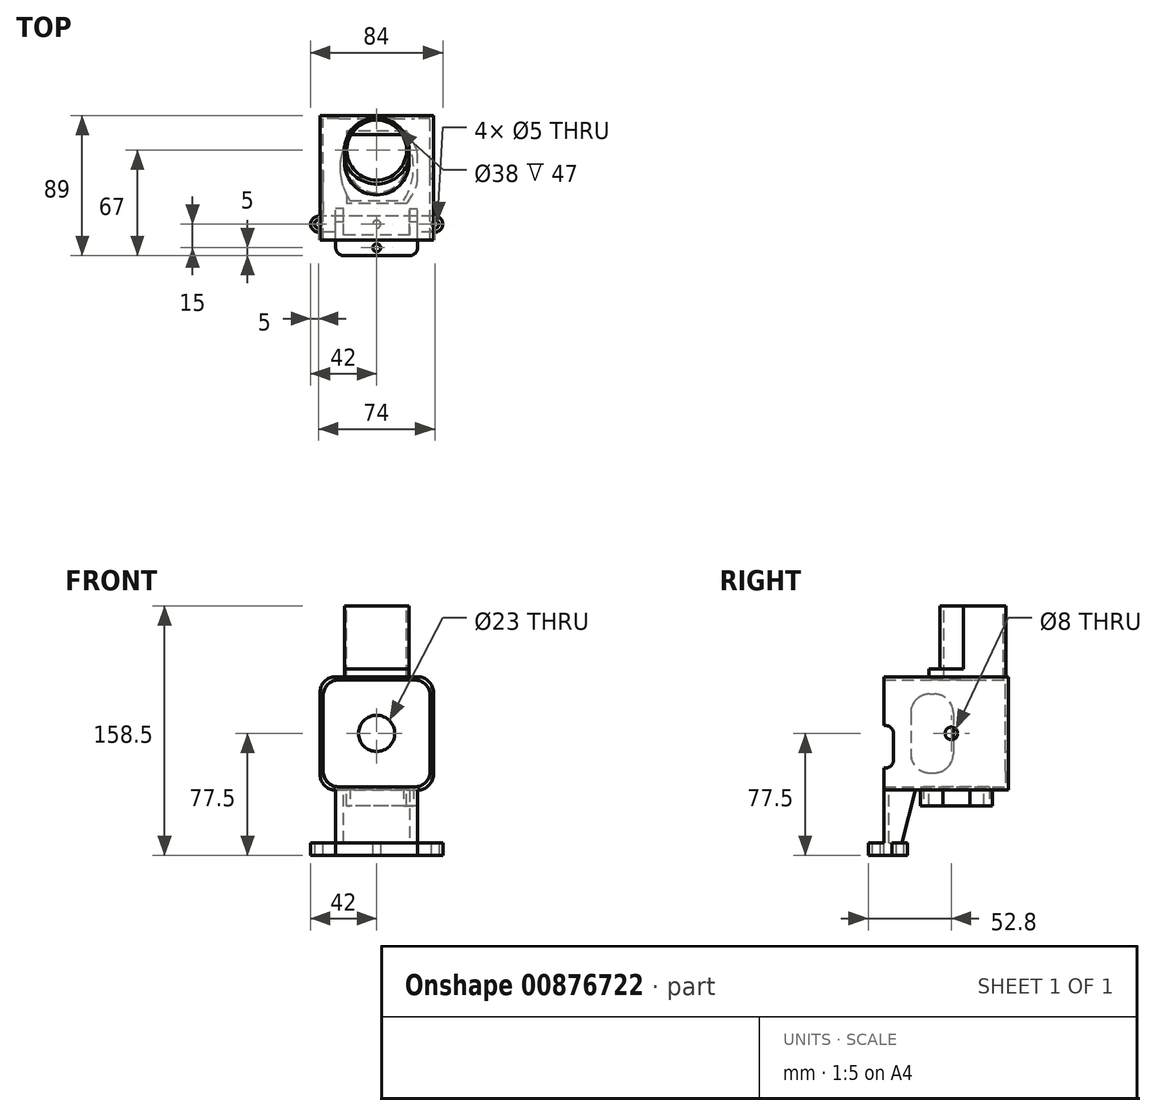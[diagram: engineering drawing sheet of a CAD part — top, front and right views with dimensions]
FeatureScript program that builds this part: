
annotation { "Feature Type Name" : "Feature", "Feature Type Description" : "" }
export const myFeature = defineFeature(function(context is Context, id is Id, definition is map)
    precondition{}
    {
        {
            var Q0;
            Q0=qCreatedBy(makeId("Front.planeOp"),FACE);
            var sketch = newSketch(context, id + "F0", { "sketchPlane" : qUnion([Q0])});
            skLineSegment(sketch, "E0.bottom", {"start": v(-24, -34) * mm, "end": v(24, -34) * mm});
            skLineSegment(sketch, "E0.top", {"start": v(-24, 34) * mm, "end": v(24, 34) * mm});
            skLineSegment(sketch, "E0.left", {"start": v(-34, -24) * mm, "end": v(-34, 24) * mm});
            skLineSegment(sketch, "E0.right", {"start": v(34, -24) * mm, "end": v(34, 24) * mm});
            skPoint(sketch, "E0.middle", {"position": v(0, 0) * mm});
            skLineSegment(sketch, "E1.bottom", {"start": v(-26, 36) * mm, "end": v(26, 36) * mm});
            skLineSegment(sketch, "E1.top", {"start": v(-26, -36) * mm, "end": v(26, -36) * mm});
            skLineSegment(sketch, "E1.left", {"start": v(-36, 26) * mm, "end": v(-36, -26) * mm});
            skLineSegment(sketch, "E1.right", {"start": v(36, 26) * mm, "end": v(36, -26) * mm});
            skCircle(sketch, "E2", {"center": v(0, 0) * mm, "radius": 11.5 * mm});
            skPoint(sketch, "E3.visualSharp", {"position": v(-36, 36) * mm});
            skArc(sketch, "E3.filletArc", {"start": v(-26, 36) * mm, "mid": v(-33.07, 33.07) * mm, "end": v(-36, 26) * mm});
            skPoint(sketch, "E4.visualSharp", {"position": v(-34, 34) * mm});
            skArc(sketch, "E4.filletArc", {"start": v(-24, 34) * mm, "mid": v(-31.07, 31.07) * mm, "end": v(-34, 24) * mm});
            skPoint(sketch, "E5.visualSharp", {"position": v(34, 34) * mm});
            skArc(sketch, "E5.filletArc", {"start": v(34, 24) * mm, "mid": v(31.07, 31.07) * mm, "end": v(24, 34) * mm});
            skPoint(sketch, "E6.visualSharp", {"position": v(36, 36) * mm});
            skArc(sketch, "E6.filletArc", {"start": v(36, 26) * mm, "mid": v(33.07, 33.07) * mm, "end": v(26, 36) * mm});
            skPoint(sketch, "E7.visualSharp", {"position": v(-34, -34) * mm});
            skArc(sketch, "E7.filletArc", {"start": v(-34, -24) * mm, "mid": v(-31.07, -31.07) * mm, "end": v(-24, -34) * mm});
            skPoint(sketch, "E8.visualSharp", {"position": v(-36, -36) * mm});
            skArc(sketch, "E8.filletArc", {"start": v(-36, -26) * mm, "mid": v(-33.07, -33.07) * mm, "end": v(-26, -36) * mm});
            skPoint(sketch, "E9.visualSharp", {"position": v(34, -34) * mm});
            skArc(sketch, "E9.filletArc", {"start": v(24, -34) * mm, "mid": v(31.07, -31.07) * mm, "end": v(34, -24) * mm});
            skPoint(sketch, "E10.visualSharp", {"position": v(36, -36) * mm});
            skArc(sketch, "E10.filletArc", {"start": v(26, -36) * mm, "mid": v(33.07, -33.07) * mm, "end": v(36, -26) * mm});
            skSolve(sketch);
        }
        {
            var Q0;
            Q0=makeQuery(id+"F0.imprint","IMPRINT",FACE,{"disambiguationData":[TD([[makeQuery(id+"F0.imprint","IMPRINT",EDGE,{"derivedFrom":sQuery(id+"F0.wireOp",EDGE,"E0.bottom")}),1.0]])]});
            var Q1;
            Q1=makeQuery(id+"F0.imprint","IMPRINT",FACE,{"disambiguationData":[TD([[makeQuery(id+"F0.imprint","IMPRINT",EDGE,{"derivedFrom":sQuery(id+"F0.wireOp",EDGE,"E0.bottom")}),-1.0]])]});
            extrude(context, id + "F1", {"entities" : qUnion([Q0, Q1]), "depth" : 2 * mm, "offsetDistance" : 25 * mm});
        }
        {
            var Q0;
            Q0=makeQuery(id+"F1.opExtrude","CAP_FACE",FACE,{"disambiguationData":[OSD([sQuery(id+"F0.wireOp",EDGE,"E1.bottom"),sQuery(id+"F0.wireOp",EDGE,"E1.top"),sQuery(id+"F0.wireOp",EDGE,"E1.left"),sQuery(id+"F0.wireOp",EDGE,"E1.right"),sQuery(id+"F0.wireOp",EDGE,"E2"),sQuery(id+"F0.wireOp",EDGE,"E3.filletArc"),sQuery(id+"F0.wireOp",EDGE,"E6.filletArc"),sQuery(id+"F0.wireOp",EDGE,"E8.filletArc"),sQuery(id+"F0.wireOp",EDGE,"E10.filletArc")])],"isStart":false});
            var sketch = newSketch(context, id + "F2", { "sketchPlane" : qUnion([Q0])});
            skLineSegment(sketch, "E11", {"start": v(-26, 36) * mm, "end": v(26, 36) * mm});
            skLineSegment(sketch, "E12", {"start": v(36, 26) * mm, "end": v(36, -26) * mm});
            skLineSegment(sketch, "E13", {"start": v(26, -36) * mm, "end": v(-26, -36) * mm});
            skLineSegment(sketch, "E14", {"start": v(-36, -26) * mm, "end": v(-36, 26) * mm});
            skLineSegment(sketch, "E15.bottom", {"start": v(-24, -34) * mm, "end": v(24, -34) * mm});
            skLineSegment(sketch, "E15.top", {"start": v(-24, 34) * mm, "end": v(24, 34) * mm});
            skLineSegment(sketch, "E15.left", {"start": v(-34, -24) * mm, "end": v(-34, 24) * mm});
            skLineSegment(sketch, "E15.right", {"start": v(34, -24) * mm, "end": v(34, 24) * mm});
            skPoint(sketch, "E15.middle", {"position": v(0, 0) * mm});
            skPoint(sketch, "E16.visualSharp", {"position": v(-34, 34) * mm});
            skArc(sketch, "E16.filletArc", {"start": v(-24, 34) * mm, "mid": v(-31.07, 31.07) * mm, "end": v(-34, 24) * mm});
            skPoint(sketch, "E17.visualSharp", {"position": v(34, 34) * mm});
            skArc(sketch, "E17.filletArc", {"start": v(34, 24) * mm, "mid": v(31.07, 31.07) * mm, "end": v(24, 34) * mm});
            skPoint(sketch, "E18.visualSharp", {"position": v(34, -34) * mm});
            skArc(sketch, "E18.filletArc", {"start": v(24, -34) * mm, "mid": v(31.07, -31.07) * mm, "end": v(34, -24) * mm});
            skPoint(sketch, "E19.visualSharp", {"position": v(-34, -34) * mm});
            skArc(sketch, "E19.filletArc", {"start": v(-34, -24) * mm, "mid": v(-31.07, -31.07) * mm, "end": v(-24, -34) * mm});
            skSolve(sketch);
        }
        {
            var Q0;
            Q0=makeQuery(id+"F2.imprint","IMPRINT",FACE,{"disambiguationData":[TD([[makeQuery(id+"F2.imprint","IMPRINT",EDGE,{"derivedFrom":sQuery(id+"F2.wireOp",EDGE,"E11")}),-1.0]])]});
            extrude(context, id + "F3", {"entities" : qUnion([Q0]), "operationType" : NewBodyOperationType.ADD, "depth" : 77 * mm, "offsetDistance" : 25 * mm});
        }
        {
            var Q0;
            Q0=makeQuery(id+"F3.boolean.opBoolean","MERGE",FACE,{"derivedFrom":[makeQuery(id+"F1.opExtrude","SWEPT_FACE",FACE,{"disambiguationData":[OSD([sQuery(id+"F0.wireOp",EDGE,"E1.left")])]}),makeQuery(id+"F3.opExtrude","SWEPT_FACE",FACE,{"disambiguationData":[OSD([sQuery(id+"F2.wireOp",EDGE,"E14")])]})]});
            var sketch = newSketch(context, id + "F4", { "sketchPlane" : qUnion([Q0])});
            skPoint(sketch, "E20.visualSharp", {"position": v(-64.19, -30) * mm});
            skLineSegment(sketch, "E21.bottom", {"start": v(50, 25) * mm, "end": v(47, 25) * mm});
            skLineSegment(sketch, "E21.top", {"start": v(50, -25) * mm, "end": v(47, -25) * mm});
            skLineSegment(sketch, "E21.left", {"start": v(62, 13) * mm, "end": v(62, -13) * mm});
            skLineSegment(sketch, "E21.right", {"start": v(35, 13) * mm, "end": v(35, -13) * mm});
            skPoint(sketch, "E21.middle", {"position": v(48.5, 0) * mm});
            skPoint(sketch, "E22.visualSharp", {"position": v(62, -25) * mm});
            skArc(sketch, "E22.filletArc", {"start": v(50, -25) * mm, "mid": v(58.49, -21.49) * mm, "end": v(62, -13) * mm});
            skPoint(sketch, "E23.visualSharp", {"position": v(35, -25) * mm});
            skArc(sketch, "E23.filletArc", {"start": v(35, -13) * mm, "mid": v(38.51, -21.49) * mm, "end": v(47, -25) * mm});
            skPoint(sketch, "E24.visualSharp", {"position": v(35, 25) * mm});
            skArc(sketch, "E24.filletArc", {"start": v(47, 25) * mm, "mid": v(38.51, 21.49) * mm, "end": v(35, 13) * mm});
            skPoint(sketch, "E25.visualSharp", {"position": v(62, 25) * mm});
            skArc(sketch, "E25.filletArc", {"start": v(62, 13) * mm, "mid": v(58.49, 21.49) * mm, "end": v(50, 25) * mm});
            skSolve(sketch);
        }
        {
            var Q0;
            Q0=makeQuery(id+"F4.imprint","IMPRINT",FACE,{"disambiguationData":[TD([[makeQuery(id+"F4.imprint","IMPRINT",EDGE,{"derivedFrom":sQuery(id+"F4.wireOp",EDGE,"E21.bottom")}),1.0]])]});
            extrude(context, id + "F5", {"entities" : qUnion([Q0]), "operationType" : NewBodyOperationType.REMOVE, "oppositeDirection" : true, "depth" : 3 * mm, "offsetDistance" : 25 * mm});
        }
        {
            var Q0;
            Q0=makeQuery(id+"F3.boolean.opBoolean","MERGE",FACE,{"derivedFrom":[makeQuery(id+"F1.opExtrude","SWEPT_FACE",FACE,{"disambiguationData":[OSD([sQuery(id+"F0.wireOp",EDGE,"E1.bottom")])]}),makeQuery(id+"F3.opExtrude","SWEPT_FACE",FACE,{"disambiguationData":[OSD([sQuery(id+"F2.wireOp",EDGE,"E11")])]})]});
            var sketch = newSketch(context, id + "F6", { "sketchPlane" : qUnion([Q0])});
            skPoint(sketch, "E26.middle", {"position": v(0, -26) * mm});
            skArc(sketch, "E27", {"start": v(19, -22) * mm, "mid": v(0, -3) * mm, "end": v(-19, -22) * mm});
            skArc(sketch, "E28", {"start": v(-19, -30) * mm, "mid": v(0, -49) * mm, "end": v(19, -30) * mm});
            skPoint(sketch, "E29.orphan", {"position": v(-19, -49) * mm});
            skPoint(sketch, "E30.orphan", {"position": v(19, -49) * mm});
            skPoint(sketch, "E31.orphan", {"position": v(19, -3) * mm});
            skPoint(sketch, "E32.orphan", {"position": v(-19, -3) * mm});
            skLineSegment(sketch, "E33", {"start": v(19, -30) * mm, "end": v(19, -22) * mm});
            skLineSegment(sketch, "E34", {"start": v(-19, -30) * mm, "end": v(-19, -22) * mm});
            skSolve(sketch);
        }
        {
            var Q0;
            Q0=makeQuery(id+"F6.imprint","IMPRINT",FACE,{"disambiguationData":[TD([[makeQuery(id+"F6.imprint","IMPRINT",EDGE,{"derivedFrom":sQuery(id+"F6.wireOp",EDGE,"E27")}),1.0]])]});
            extrude(context, id + "F7", {"entities" : qUnion([Q0]), "operationType" : NewBodyOperationType.REMOVE, "oppositeDirection" : true, "depth" : 3 * mm, "offsetDistance" : 25 * mm});
        }
        {
            var Q0;
            Q0=makeQuery(id+"F3.boolean.opBoolean","MERGE",FACE,{"derivedFrom":[makeQuery(id+"F1.opExtrude","SWEPT_FACE",FACE,{"disambiguationData":[OSD([sQuery(id+"F0.wireOp",EDGE,"E1.bottom")])]}),makeQuery(id+"F3.opExtrude","SWEPT_FACE",FACE,{"disambiguationData":[OSD([sQuery(id+"F2.wireOp",EDGE,"E11")])]})]});
            var sketch = newSketch(context, id + "F8", { "sketchPlane" : qUnion([Q0])});
            skArc(sketch, "E35", {"start": v(19, -22) * mm, "mid": v(0, -3) * mm, "end": v(-19, -22) * mm});
            skArc(sketch, "E36", {"start": v(-19, -30) * mm, "mid": v(0, -49) * mm, "end": v(19, -30) * mm});
            skLineSegment(sketch, "E37", {"start": v(-19, -30) * mm, "end": v(-19, -22) * mm});
            skLineSegment(sketch, "E38", {"start": v(19, -30) * mm, "end": v(19, -29.7) * mm});
            skArc(sketch, "E39", {"start": v(-20.5, -30) * mm, "mid": v(0, -50.5) * mm, "end": v(20.5, -30) * mm});
            skArc(sketch, "E40", {"start": v(20.5, -22) * mm, "mid": v(0, -1.5) * mm, "end": v(-20.5, -22) * mm});
            skLineSegment(sketch, "E41", {"start": v(20.5, -30) * mm, "end": v(20.5, -22) * mm});
            skLineSegment(sketch, "E42", {"start": v(-20.5, -30) * mm, "end": v(-20.5, -22) * mm});
            skLineSegment(sketch, "E43.trimOffspring", {"start": v(19, -22.3) * mm, "end": v(19, -22) * mm});
            skSolve(sketch);
        }
        {
            var Q0;
            Q0=makeQuery(id+"F8.imprint","IMPRINT",FACE,{"disambiguationData":[TD([[makeQuery(id+"F8.imprint","IMPRINT",EDGE,{"derivedFrom":sQuery(id+"F8.wireOp",EDGE,"E35")}),-1.0]])]});
            var Q1;
            Q1=makeQuery(id+"F8.imprint","IMPRINT",FACE,{"disambiguationData":[TD([[makeQuery(id+"F8.imprint","IMPRINT",EDGE,{"derivedFrom":sQuery(id+"F8.wireOp",EDGE,"E35")}),1.0]])]});
            extrude(context, id + "F9", {"entities" : qUnion([Q0, Q1]), "operationType" : NewBodyOperationType.ADD, "depth" : 5 * mm, "offsetDistance" : 25 * mm});
        }
        {
            var Q0;
            Q0=makeQuery(id+"F3.boolean.opBoolean","MERGE",FACE,{"derivedFrom":[makeQuery(id+"F1.opExtrude","SWEPT_FACE",FACE,{"disambiguationData":[OSD([sQuery(id+"F0.wireOp",EDGE,"E1.bottom")])]}),makeQuery(id+"F3.opExtrude","SWEPT_FACE",FACE,{"disambiguationData":[OSD([sQuery(id+"F2.wireOp",EDGE,"E11")])]})]});
            var sketch = newSketch(context, id + "F10", { "sketchPlane" : qUnion([Q0])});
            skArc(sketch, "E44", {"start": v(20.5, -22) * mm, "mid": v(0, -1.5) * mm, "end": v(-20.5, -22) * mm});
            skArc(sketch, "E45", {"start": v(-20.5, -30) * mm, "mid": v(0, -50.5) * mm, "end": v(20.5, -30) * mm});
            skLineSegment(sketch, "E46", {"start": v(-20.5, -30) * mm, "end": v(-20.5, -22) * mm});
            skLineSegment(sketch, "E47", {"start": v(20.5, -30) * mm, "end": v(20.5, -22) * mm});
            skSolve(sketch);
        }
        {
            var Q0;
            Q0=makeQuery(id+"F10.imprint","IMPRINT",FACE,{"disambiguationData":[TD([[makeQuery(id+"F10.imprint","IMPRINT",EDGE,{"derivedFrom":sQuery(id+"F10.wireOp",EDGE,"E44")}),1.0]])]});
            extrude(context, id + "F11", {"entities" : qUnion([Q0]), "operationType" : NewBodyOperationType.ADD, "depth" : 3 * mm, "offsetDistance" : 25 * mm});
        }
        {
            var Q0;
            Q0=makeQuery(id+"F9.opExtrude","CAP_FACE",FACE,{"disambiguationData":[OSD([sQuery(id+"F8.wireOp",EDGE,"E39"),sQuery(id+"F8.wireOp",EDGE,"E40"),sQuery(id+"F8.wireOp",EDGE,"E41"),sQuery(id+"F8.wireOp",EDGE,"E42")])],"isStart":false});
            var sketch = newSketch(context, id + "F12", { "sketchPlane" : qUnion([Q0])});
            skCircle(sketch, "E48", {"center": v(0, -22) * mm, "radius": 19 * mm});
            skPoint(sketch, "E49.center.orphan", {"position": v(0, -19.52) * mm});
            skPoint(sketch, "E50.center.orphan", {"position": v(0, -18.76) * mm});
            skSolve(sketch);
        }
        {
            var Q0;
            Q0=makeQuery(id+"F12.imprint","IMPRINT",FACE,{"disambiguationData":[TD([[makeQuery(id+"F12.imprint","IMPRINT",EDGE,{"derivedFrom":sQuery(id+"F12.wireOp",EDGE,"E48")}),1.0]])]});
            extrude(context, id + "F13", {"entities" : qUnion([Q0]), "operationType" : NewBodyOperationType.REMOVE, "oppositeDirection" : true, "depth" : 8 * mm, "offsetDistance" : 25 * mm});
        }
        {
            var Q0;
            Q0=makeQuery(id+"F9.opExtrude","CAP_FACE",FACE,{"disambiguationData":[OSD([sQuery(id+"F8.wireOp",EDGE,"E39"),sQuery(id+"F8.wireOp",EDGE,"E40"),sQuery(id+"F8.wireOp",EDGE,"E41"),sQuery(id+"F8.wireOp",EDGE,"E42")])],"isStart":false});
            var sketch = newSketch(context, id + "F14", { "sketchPlane" : qUnion([Q0])});
            skCircle(sketch, "E51", {"center": v(0, -22) * mm, "radius": 19 * mm});
            skCircle(sketch, "E52", {"center": v(0, -22) * mm, "radius": 21.5 * mm});
            skSolve(sketch);
        }
        {
            var Q0;
            Q0=makeQuery(id+"F14.imprint","IMPRINT",FACE,{"disambiguationData":[TD([[makeQuery(id+"F14.imprint","IMPRINT",EDGE,{"derivedFrom":sQuery(id+"F14.wireOp",EDGE,"E51")}),-1.0]])]});
            extrude(context, id + "F15", {"entities" : qUnion([Q0]), "operationType" : NewBodyOperationType.ADD, "depth" : 40 * mm, "offsetDistance" : 25 * mm});
        }
        {
            var Q0;
            Q0=makeQuery(id+"F3.boolean.opBoolean","MERGE",FACE,{"derivedFrom":[makeQuery(id+"F1.opExtrude","SWEPT_FACE",FACE,{"disambiguationData":[OSD([sQuery(id+"F0.wireOp",EDGE,"E1.top")])]}),makeQuery(id+"F3.opExtrude","SWEPT_FACE",FACE,{"disambiguationData":[OSD([sQuery(id+"F2.wireOp",EDGE,"E13")])]})]});
            var sketch = newSketch(context, id + "F16", { "sketchPlane" : qUnion([Q0])});
            skLineSegment(sketch, "E53.bottom", {"start": v(26, 79) * mm, "end": v(-26, 79) * mm});
            skLineSegment(sketch, "E53.top", {"start": v(26, 76) * mm, "end": v(-26, 76) * mm});
            skLineSegment(sketch, "E53.left", {"start": v(26, 79) * mm, "end": v(26, 76) * mm});
            skLineSegment(sketch, "E53.right", {"start": v(-26, 79) * mm, "end": v(-26, 76) * mm});
            skSolve(sketch);
        }
        {
            var Q0;
            Q0=makeQuery(id+"F16.imprint","IMPRINT",FACE,{"disambiguationData":[TD([[makeQuery(id+"F16.imprint","IMPRINT",EDGE,{"derivedFrom":sQuery(id+"F16.wireOp",EDGE,"E53.bottom")}),-1.0]])]});
            extrude(context, id + "F17", {"entities" : qUnion([Q0]), "operationType" : NewBodyOperationType.ADD, "depth" : 38.5 * mm, "offsetDistance" : 25 * mm});
        }
        {
            var Q0;
            Q0=makeQuery(id+"F3.boolean.opBoolean","MERGE",FACE,{"derivedFrom":[makeQuery(id+"F1.opExtrude","SWEPT_FACE",FACE,{"disambiguationData":[OSD([sQuery(id+"F0.wireOp",EDGE,"E1.top")])]}),makeQuery(id+"F3.opExtrude","SWEPT_FACE",FACE,{"disambiguationData":[OSD([sQuery(id+"F2.wireOp",EDGE,"E13")])]})]});
            var sketch = newSketch(context, id + "F18", { "sketchPlane" : qUnion([Q0])});
            skLineSegment(sketch, "E54.bottom", {"start": v(17, 12) * mm, "end": v(-17, 12) * mm});
            skLineSegment(sketch, "E54.top", {"start": v(17, 54) * mm, "end": v(-17, 54) * mm});
            skPoint(sketch, "E54.middle", {"position": v(0, 33) * mm});
            skArc(sketch, "E55", {"start": v(17, 12) * mm, "mid": v(23.33, 33) * mm, "end": v(17, 54) * mm});
            skArc(sketch, "E56", {"start": v(-17, 54) * mm, "mid": v(-23.33, 33) * mm, "end": v(-17, 12) * mm});
            skSolve(sketch);
        }
        {
            var Q0;
            Q0=makeQuery(id+"F18.imprint","IMPRINT",FACE,{"disambiguationData":[TD([[makeQuery(id+"F18.imprint","IMPRINT",EDGE,{"derivedFrom":sQuery(id+"F18.wireOp",EDGE,"E54.bottom")}),-1.0]])]});
            extrude(context, id + "F19", {"entities" : qUnion([Q0]), "operationType" : NewBodyOperationType.REMOVE, "oppositeDirection" : true, "depth" : 3 * mm, "offsetDistance" : 25 * mm});
        }
        {
            var Q0;
            Q0=makeQuery(id+"F3.boolean.opBoolean","MERGE",FACE,{"derivedFrom":[makeQuery(id+"F1.opExtrude","SWEPT_FACE",FACE,{"disambiguationData":[OSD([sQuery(id+"F0.wireOp",EDGE,"E1.top")])]}),makeQuery(id+"F3.opExtrude","SWEPT_FACE",FACE,{"disambiguationData":[OSD([sQuery(id+"F2.wireOp",EDGE,"E13")])]})]});
            var sketch = newSketch(context, id + "F20", { "sketchPlane" : qUnion([Q0])});
            skLineSegment(sketch, "E57.bottom", {"start": v(-17, 12) * mm, "end": v(17, 12) * mm});
            skLineSegment(sketch, "E57.top", {"start": v(-17, 54) * mm, "end": v(17, 54) * mm});
            skPoint(sketch, "E57.middle", {"position": v(0, 33) * mm});
            skPoint(sketch, "E57.middle.positionSnap0", {"position": v(0, 12) * mm});
            skPoint(sketch, "E57.centerSnap0", {"position": v(0, 12) * mm});
            skArc(sketch, "E58", {"start": v(17, 12) * mm, "mid": v(23.33, 33) * mm, "end": v(17, 54) * mm});
            skArc(sketch, "E59", {"start": v(-17, 54) * mm, "mid": v(-23.33, 33) * mm, "end": v(-17, 12) * mm});
            skLineSegment(sketch, "E60.bottom", {"start": v(19, 10) * mm, "end": v(-19, 10) * mm});
            skLineSegment(sketch, "E60.top", {"start": v(19, 56) * mm, "end": v(-19, 56) * mm});
            skLineSegment(sketch, "E60.left", {"start": v(19, 10) * mm, "end": v(19, 56) * mm});
            skLineSegment(sketch, "E60.right", {"start": v(-19, 10) * mm, "end": v(-19, 56) * mm});
            skArc(sketch, "E61", {"start": v(19, 10) * mm, "mid": v(27.02, 33) * mm, "end": v(19, 56) * mm});
            skArc(sketch, "E62", {"start": v(-19, 56) * mm, "mid": v(-27.02, 33) * mm, "end": v(-19, 10) * mm});
            skSolve(sketch);
        }
        {
            var Q0;
            {var subQ1=sQuery(id+"F20.wireOp",EDGE,"E60.left");var subQ7=sQuery(id+"F20.wireOp",EDGE,"E58");var subQ9=makeQuery(id+"F20.imprint","INTERSECT",VERTEX,{"disambiguationData":[OD(0.0)],"derivedFrom":[subQ7,subQ1]});Q0=makeQuery(id+"F20.imprint","IMPRINT",FACE,{"disambiguationData":[TD([[makeQuery(id+"F20.imprint","IMPRINT",EDGE,{"disambiguationData":[TD([[subQ9,-1.0]])],"derivedFrom":subQ7}),-1.0]])]});}
            var Q1;
            {var subQ1=sQuery(id+"F20.wireOp",EDGE,"E57.top");Q1=makeQuery(id+"F20.imprint","IMPRINT",FACE,{"disambiguationData":[TD([[makeQuery(id+"F20.imprint","IMPRINT",EDGE,{"derivedFrom":subQ1}),-1.0]])]});}
            var Q2;
            {var subQ1=sQuery(id+"F20.wireOp",EDGE,"E60.right");var subQ6=sQuery(id+"F20.wireOp",EDGE,"E59");var subQ7=makeQuery(id+"F20.imprint","INTERSECT",VERTEX,{"disambiguationData":[OD(0.0)],"derivedFrom":[subQ6,subQ1]});Q2=makeQuery(id+"F20.imprint","IMPRINT",FACE,{"disambiguationData":[TD([[makeQuery(id+"F20.imprint","IMPRINT",EDGE,{"disambiguationData":[TD([[subQ7,-1.0]])],"derivedFrom":subQ6}),-1.0]])]});}
            var Q3;
            {var subQ2=sQuery(id+"F20.wireOp",EDGE,"E57.bottom");Q3=makeQuery(id+"F20.imprint","IMPRINT",FACE,{"disambiguationData":[TD([[makeQuery(id+"F20.imprint","IMPRINT",EDGE,{"derivedFrom":subQ2}),1.0]])]});}
            extrude(context, id + "F21", {"entities" : qUnion([Q0, Q1, Q2, Q3]), "operationType" : NewBodyOperationType.ADD, "depth" : 10 * mm, "offsetDistance" : 25 * mm});
        }
        {
            var Q0;
            Q0=makeQuery(id+"F17.opExtrude","SWEPT_FACE",FACE,{"disambiguationData":[OSD([sQuery(id+"F16.wireOp",EDGE,"E53.left")])]});
            var sketch = newSketch(context, id + "F22", { "sketchPlane" : qUnion([Q0])});
            skLineSegment(sketch, "E63", {"start": v(-79, -74.5) * mm, "end": v(-69, -74.5) * mm});
            skLineSegment(sketch, "E64", {"start": v(-69, -74.5) * mm, "end": v(-59, -36) * mm});
            skLineSegment(sketch, "E65", {"start": v(-59, -36) * mm, "end": v(-79, -36) * mm});
            skLineSegment(sketch, "E66", {"start": v(-79, -36) * mm, "end": v(-79, -74.5) * mm});
            skSolve(sketch);
        }
        {
            var Q0;
            {var subQ2=sQuery(id+"F22.wireOp",EDGE,"E64");Q0=makeQuery(id+"F22.imprint","IMPRINT",FACE,{"disambiguationData":[TD([[makeQuery(id+"F22.imprint","IMPRINT",EDGE,{"derivedFrom":subQ2}),1.0]])]});}
            var Q1;
            {var subQ0=sQuery(id+"F22.wireOp",EDGE,"E66");Q1=makeQuery(id+"F22.imprint","IMPRINT",FACE,{"disambiguationData":[TD([[makeQuery(id+"F22.imprint","IMPRINT",EDGE,{"derivedFrom":subQ0}),-1.0]])]});}
            extrude(context, id + "F23", {"entities" : qUnion([Q0, Q1]), "operationType" : NewBodyOperationType.ADD, "oppositeDirection" : true, "depth" : 5 * mm, "offsetDistance" : 25 * mm});
        }
        {
            var Q0;
            Q0=makeQuery(id+"F17.opExtrude","SWEPT_FACE",FACE,{"disambiguationData":[OSD([sQuery(id+"F16.wireOp",EDGE,"E53.right")])]});
            var sketch = newSketch(context, id + "F24", { "sketchPlane" : qUnion([Q0])});
            skLineSegment(sketch, "E67", {"start": v(79, -74.5) * mm, "end": v(69, -74.5) * mm});
            skLineSegment(sketch, "E68", {"start": v(69, -74.5) * mm, "end": v(59, -36) * mm});
            skLineSegment(sketch, "E69", {"start": v(59, -36) * mm, "end": v(79, -36) * mm});
            skLineSegment(sketch, "E70", {"start": v(79, -36) * mm, "end": v(79, -74.5) * mm});
            skSolve(sketch);
        }
        {
            var Q0;
            Q0=makeQuery(id+"FvH5MofawmtUx0a_1.boolean.opBoolean","MERGE",FACE,{"derivedFrom":[makeQuery(id+"F23.boolean.opBoolean","MERGE",FACE,{"derivedFrom":[makeQuery(id+"F17.opExtrude","CAP_FACE",FACE,{"disambiguationData":[OSD([sQuery(id+"F16.wireOp",EDGE,"E53.bottom"),sQuery(id+"F16.wireOp",EDGE,"E53.top"),sQuery(id+"F16.wireOp",EDGE,"E53.left"),sQuery(id+"F16.wireOp",EDGE,"E53.right")])],"isStart":false}),makeQuery(id+"F23.opExtrude","SWEPT_FACE",FACE,{"disambiguationData":[OSD([sQuery(id+"F22.wireOp",EDGE,"E63")])]})]}),makeQuery(id+"FvH5MofawmtUx0a_1.opExtrude","SWEPT_FACE",FACE,{"disambiguationData":[OSD([sQuery(id+"F24.wireOp",EDGE,"E67")])]})]});
            var sketch = newSketch(context, id + "F25", { "sketchPlane" : qUnion([Q0])});
            skLineSegment(sketch, "E71.bottom", {"start": v(-26, 79) * mm, "end": v(26, 79) * mm});
            skLineSegment(sketch, "E71.top", {"start": v(-26, 74) * mm, "end": v(26, 74) * mm});
            skLineSegment(sketch, "E71.left", {"start": v(-26, 79) * mm, "end": v(-26, 74) * mm});
            skLineSegment(sketch, "E71.right", {"start": v(26, 79) * mm, "end": v(26, 74) * mm});
            skLineSegment(sketch, "E72.bottom", {"start": v(37, 64) * mm, "end": v(-37, 64) * mm});
            skLineSegment(sketch, "E72.top", {"start": v(37, 74) * mm, "end": v(-37, 74) * mm});
            skPoint(sketch, "E72.middle", {"position": v(0, 69) * mm});
            skCircle(sketch, "E73", {"center": v(37, 69) * mm, "radius": 2.5 * mm});
            skCircle(sketch, "E74", {"center": v(-37, 69) * mm, "radius": 2.5 * mm});
            skCircle(sketch, "E75", {"center": v(0, 69) * mm, "radius": 2.5 * mm});
            skArc(sketch, "E76", {"start": v(37, 64) * mm, "mid": v(42, 69) * mm, "end": v(37, 74) * mm});
            skArc(sketch, "E77", {"start": v(-37, 74) * mm, "mid": v(-42, 69) * mm, "end": v(-37, 64) * mm});
            skPoint(sketch, "E78.orphan", {"position": v(50, 64) * mm});
            skPoint(sketch, "E72.left.end.orphan", {"position": v(50, 74) * mm});
            skPoint(sketch, "E79.orphan", {"position": v(-50, 64) * mm});
            skPoint(sketch, "E80.orphan", {"position": v(-50, 74) * mm});
            skLineSegment(sketch, "E81.bottom", {"start": v(26, 79) * mm, "end": v(-26.03, 79) * mm});
            skLineSegment(sketch, "E81.top", {"start": v(21, 89) * mm, "end": v(-21.03, 89) * mm});
            skLineSegment(sketch, "E81.left", {"start": v(26, 79) * mm, "end": v(26, 84) * mm});
            skLineSegment(sketch, "E81.right", {"start": v(-26.03, 79) * mm, "end": v(-26.03, 84) * mm});
            skPoint(sketch, "E82.visualSharp", {"position": v(26, 89) * mm});
            skArc(sketch, "E82.filletArc", {"start": v(26, 84) * mm, "mid": v(24.54, 87.54) * mm, "end": v(21, 89) * mm});
            skPoint(sketch, "E83.visualSharp", {"position": v(-26.03, 89) * mm});
            skArc(sketch, "E83.filletArc", {"start": v(-21.03, 89) * mm, "mid": v(-24.57, 87.54) * mm, "end": v(-26.03, 84) * mm});
            skCircle(sketch, "E84", {"center": v(0, 84) * mm, "radius": 2.5 * mm});
            skSolve(sketch);
        }
        {
            var Q0;
            Q0=makeQuery(id+"F25.imprint","IMPRINT",FACE,{"disambiguationData":[TD([[makeQuery(id+"F25.imprint","IMPRINT",EDGE,{"derivedFrom":sQuery(id+"F25.wireOp",EDGE,"E72.bottom")}),-1.0]])]});
            var Q1;
            Q1=makeQuery(id+"F25.imprint","IMPRINT",FACE,{"disambiguationData":[TD([[makeQuery(id+"F25.imprint","IMPRINT",EDGE,{"derivedFrom":sQuery(id+"F25.wireOp",EDGE,"E71.bottom")}),-1.0]])]});
            var Q2;
            {var subQ1=sQuery(id+"F22.wireOp",EDGE,"E63");var subQ2=makeQuery(id+"F23.opExtrude","CAP_EDGE",EDGE,{"disambiguationData":[OSD([subQ1])],"isStart":false});Q2=makeQuery(id+"F25.imprint","IMPRINT",FACE,{"disambiguationData":[TD([[makeQuery(id+"F25.imprint","IMPRINT",EDGE,{"derivedFrom":subQ2}),1.0]])]});}
            var Q3;
            {var subQ1=sQuery(id+"F24.wireOp",EDGE,"E67");var subQ2=makeQuery(id+"FvH5MofawmtUx0a_1.opExtrude","CAP_EDGE",EDGE,{"disambiguationData":[OSD([subQ1])],"isStart":false});Q3=makeQuery(id+"F25.imprint","IMPRINT",FACE,{"disambiguationData":[TD([[makeQuery(id+"F25.imprint","IMPRINT",EDGE,{"derivedFrom":subQ2}),-1.0]])]});}
            var Q4;
            {var subQ5=makeQuery(id+"F17.opExtrude","CAP_EDGE",EDGE,{"disambiguationData":[OSD([sQuery(id+"F16.wireOp",EDGE,"E53.top")])],"isStart":false});Q4=makeQuery(id+"F25.imprint","IMPRINT",FACE,{"disambiguationData":[TD([[makeQuery(id+"F25.imprint","IMPRINT",EDGE,{"derivedFrom":subQ5}),1.0]])]});}
            var Q5;
            Q5=makeQuery(id+"F25.imprint","IMPRINT",FACE,{"disambiguationData":[TD([[makeQuery(id+"F25.imprint","IMPRINT",EDGE,{"derivedFrom":sQuery(id+"F25.wireOp",EDGE,"E81.top")}),1.0]])]});
            extrude(context, id + "F26", {"entities" : qUnion([Q0, Q1, Q2, Q3, Q4, Q5]), "operationType" : NewBodyOperationType.ADD, "oppositeDirection" : true, "depth" : 5 * mm, "offsetDistance" : 25 * mm});
        }
        {
            var Q0;
            Q0=makeQuery(id+"F26.boolean.opBoolean","MERGE",FACE,{"derivedFrom":[makeQuery(id+"FvH5MofawmtUx0a_1.boolean.opBoolean","MERGE",FACE,{"derivedFrom":[makeQuery(id+"F23.boolean.opBoolean","MERGE",FACE,{"derivedFrom":[makeQuery(id+"F17.opExtrude","CAP_FACE",FACE,{"disambiguationData":[OSD([sQuery(id+"F16.wireOp",EDGE,"E53.bottom"),sQuery(id+"F16.wireOp",EDGE,"E53.top"),sQuery(id+"F16.wireOp",EDGE,"E53.left"),sQuery(id+"F16.wireOp",EDGE,"E53.right")])],"isStart":false}),makeQuery(id+"F23.opExtrude","SWEPT_FACE",FACE,{"disambiguationData":[OSD([sQuery(id+"F22.wireOp",EDGE,"E63")])]})]}),makeQuery(id+"FvH5MofawmtUx0a_1.opExtrude","SWEPT_FACE",FACE,{"disambiguationData":[OSD([sQuery(id+"F24.wireOp",EDGE,"E67")])]})]}),makeQuery(id+"F26.opExtrude","CAP_FACE",FACE,{"disambiguationData":[OSD([sQuery(id+"F25.wireOp",EDGE,"E71.bottom"),sQuery(id+"F25.wireOp",EDGE,"E71.left"),sQuery(id+"F25.wireOp",EDGE,"E71.right"),sQuery(id+"F25.wireOp",EDGE,"E72.bottom"),sQuery(id+"F25.wireOp",EDGE,"E72.top"),sQuery(id+"F25.wireOp",EDGE,"E73"),sQuery(id+"F25.wireOp",EDGE,"E74"),sQuery(id+"F25.wireOp",EDGE,"E75"),sQuery(id+"F25.wireOp",EDGE,"E76"),sQuery(id+"F25.wireOp",EDGE,"E77")])],"isStart":true})]});
            extrude(context, id + "F27", {"entities" : qUnion([Q0]), "operationType" : NewBodyOperationType.ADD, "depth" : 1 * mm, "offsetDistance" : 25 * mm});
        }
        {
            var Q0;
            Q0=makeQuery(id+"F3.boolean.opBoolean","MERGE",FACE,{"derivedFrom":[makeQuery(id+"F1.opExtrude","SWEPT_FACE",FACE,{"disambiguationData":[OSD([sQuery(id+"F0.wireOp",EDGE,"E1.right")])]}),makeQuery(id+"F3.opExtrude","SWEPT_FACE",FACE,{"disambiguationData":[OSD([sQuery(id+"F2.wireOp",EDGE,"E12")])]})]});
            var sketch = newSketch(context, id + "F28", { "sketchPlane" : qUnion([Q0])});
            skLineSegment(sketch, "E85.bottom", {"start": v(-79, 5) * mm, "end": v(-78, 5) * mm});
            skLineSegment(sketch, "E85.top", {"start": v(-79, -22) * mm, "end": v(-78, -22) * mm});
            skLineSegment(sketch, "E85.left", {"start": v(-79, 5) * mm, "end": v(-79, -22) * mm});
            skLineSegment(sketch, "E85.right", {"start": v(-73, 0) * mm, "end": v(-73, -17) * mm});
            skPoint(sketch, "E86.visualSharp", {"position": v(-73, 5) * mm});
            skArc(sketch, "E86.filletArc", {"start": v(-73, 0) * mm, "mid": v(-74.46, 3.54) * mm, "end": v(-78, 5) * mm});
            skPoint(sketch, "E87.visualSharp", {"position": v(-73, -22) * mm});
            skArc(sketch, "E87.filletArc", {"start": v(-78, -22) * mm, "mid": v(-74.46, -20.54) * mm, "end": v(-73, -17) * mm});
            skSolve(sketch);
        }
        {
            var Q0;
            Q0=makeQuery(id+"F28.imprint","IMPRINT",FACE,{"disambiguationData":[TD([[makeQuery(id+"F28.imprint","IMPRINT",EDGE,{"derivedFrom":sQuery(id+"F28.wireOp",EDGE,"E85.bottom")}),-1.0]])]});
            extrude(context, id + "F29", {"entities" : qUnion([Q0]), "operationType" : NewBodyOperationType.REMOVE, "oppositeDirection" : true, "depth" : 75 * mm, "offsetDistance" : 25 * mm});
        }
        {
            var Q0;
            Q0=makeQuery(id+"F27.opExtrude","CAP_FACE",FACE,{"disambiguationData":[OSD([sQuery(id+"F16.wireOp",EDGE,"E53.bottom"),sQuery(id+"F16.wireOp",EDGE,"E53.top"),sQuery(id+"F16.wireOp",EDGE,"E53.left"),sQuery(id+"F16.wireOp",EDGE,"E53.right"),sQuery(id+"F22.wireOp",EDGE,"E63"),sQuery(id+"F25.wireOp",EDGE,"E71.left"),sQuery(id+"F25.wireOp",EDGE,"E72.bottom"),sQuery(id+"F25.wireOp",EDGE,"E72.top"),sQuery(id+"F25.wireOp",EDGE,"E73"),sQuery(id+"F25.wireOp",EDGE,"E74"),sQuery(id+"F25.wireOp",EDGE,"E75"),sQuery(id+"F25.wireOp",EDGE,"E76"),sQuery(id+"F25.wireOp",EDGE,"E77"),sQuery(id+"F25.wireOp",EDGE,"E81.bottom"),sQuery(id+"F25.wireOp",EDGE,"E81.top"),sQuery(id+"F25.wireOp",EDGE,"E81.left"),sQuery(id+"F25.wireOp",EDGE,"E81.right"),sQuery(id+"F25.wireOp",EDGE,"E82.filletArc"),sQuery(id+"F25.wireOp",EDGE,"E83.filletArc"),sQuery(id+"F25.wireOp",EDGE,"E84")])],"isStart":false});
            extrude(context, id + "F30", {"entities" : qUnion([Q0]), "operationType" : NewBodyOperationType.ADD, "depth" : 2 * mm, "offsetDistance" : 25 * mm});
        }
        {
            var Q0;
            {var subQ0=sQuery(id+"F24.wireOp",EDGE,"E70");Q0=makeQuery(id+"F24.imprint","IMPRINT",FACE,{"disambiguationData":[TD([[makeQuery(id+"F24.imprint","IMPRINT",EDGE,{"derivedFrom":subQ0}),1.0]])]});}
            var Q1;
            {var subQ2=sQuery(id+"F24.wireOp",EDGE,"E68");Q1=makeQuery(id+"F24.imprint","IMPRINT",FACE,{"disambiguationData":[TD([[makeQuery(id+"F24.imprint","IMPRINT",EDGE,{"derivedFrom":subQ2}),-1.0]])]});}
            extrude(context, id + "F31", {"entities" : qUnion([Q0, Q1]), "operationType" : NewBodyOperationType.ADD, "oppositeDirection" : true, "depth" : 5 * mm, "offsetDistance" : 25 * mm});
        }
        {
            var Q0;
            Q0=makeQuery(id+"F3.boolean.opBoolean","MERGE",FACE,{"derivedFrom":[makeQuery(id+"F1.opExtrude","SWEPT_FACE",FACE,{"disambiguationData":[OSD([sQuery(id+"F0.wireOp",EDGE,"E1.right")])]}),makeQuery(id+"F3.opExtrude","SWEPT_FACE",FACE,{"disambiguationData":[OSD([sQuery(id+"F2.wireOp",EDGE,"E12")])]})]});
            var sketch = newSketch(context, id + "F32", { "sketchPlane" : qUnion([Q0])});
            skCircle(sketch, "E88", {"center": v(-36.2, 0) * mm, "radius": 4 * mm});
            skSolve(sketch);
        }
        {
            var Q0;
            Q0=makeQuery(id+"F32.imprint","IMPRINT",FACE,{"disambiguationData":[TD([[makeQuery(id+"F32.imprint","IMPRINT",EDGE,{"derivedFrom":sQuery(id+"F32.wireOp",EDGE,"E88")}),1.0]])]});
            extrude(context, id + "F33", {"entities" : qUnion([Q0]), "operationType" : NewBodyOperationType.REMOVE, "oppositeDirection" : true, "depth" : 3 * mm, "offsetDistance" : 25 * mm});
        }
    });
